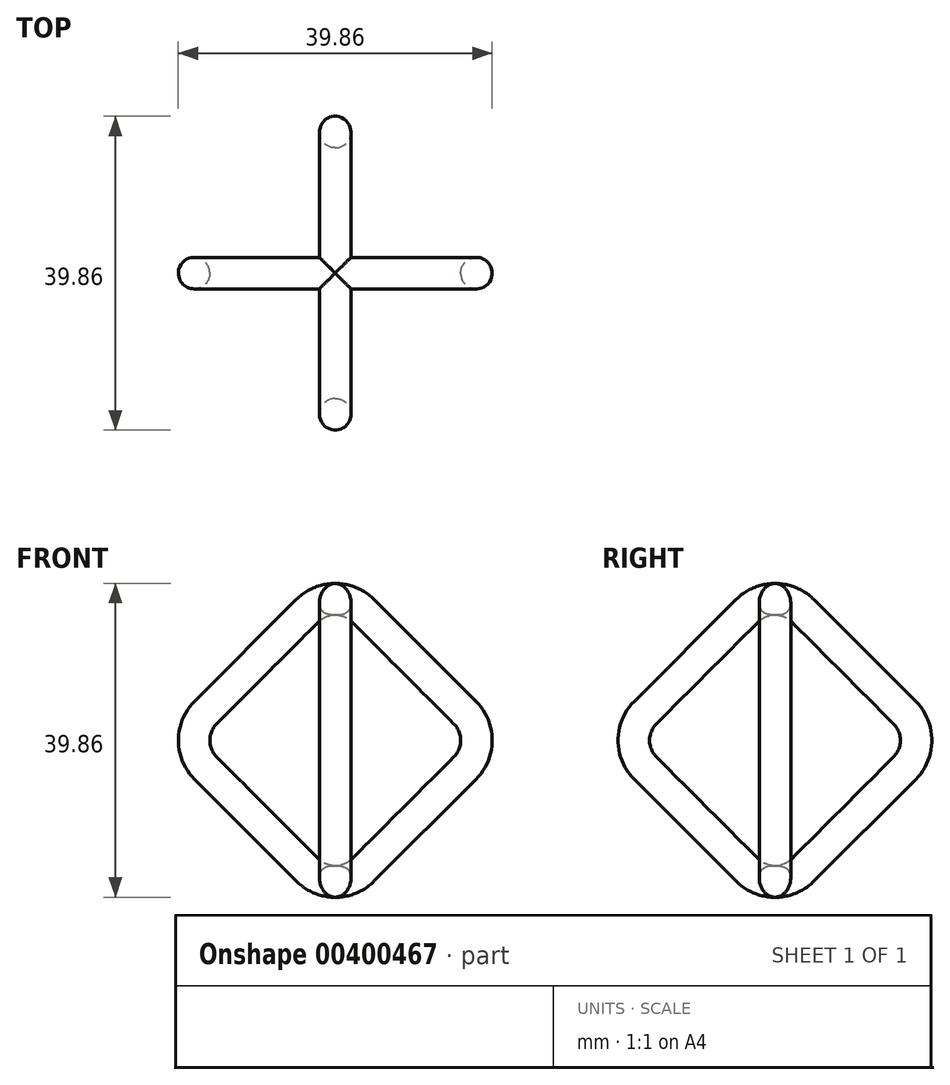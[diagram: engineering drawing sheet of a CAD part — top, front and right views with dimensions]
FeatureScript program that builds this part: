
annotation { "Feature Type Name" : "Feature", "Feature Type Description" : "" }
export const myFeature = defineFeature(function(context is Context, id is Id, definition is map)
    precondition{}
    {
        {
            var Q0;
            Q0=qCreatedBy(makeId("Front.planeOp"),FACE);
            var sketch = newSketch(context, id + "F0", { "sketchPlane" : qUnion([Q0])});
            skLineSegment(sketch, "E0", {"start": v(-3.54, 16.46) * mm, "end": v(-16.46, 3.54) * mm});
            skLineSegment(sketch, "E1", {"start": v(16.46, 3.54) * mm, "end": v(3.54, 16.46) * mm});
            skLineSegment(sketch, "E2", {"start": v(-20, 0) * mm, "end": v(20, 0) * mm, "construction": true});
            skPoint(sketch, "E3.visualSharp", {"position": v(0, 20) * mm});
            skArc(sketch, "E3.filletArc", {"start": v(3.54, 16.46) * mm, "mid": v(0, 17.93) * mm, "end": v(-3.54, 16.46) * mm});
            skPoint(sketch, "E4.visualSharp", {"position": v(20, 0) * mm});
            skArc(sketch, "E4.filletArc", {"start": v(17.93, 0) * mm, "mid": v(17.55, 1.91) * mm, "end": v(16.46, 3.54) * mm});
            skPoint(sketch, "E5.visualSharp", {"position": v(0, -20) * mm});
            skPoint(sketch, "E6.visualSharp", {"position": v(-20, 0) * mm});
            skArc(sketch, "E6.filletArc", {"start": v(-16.46, 3.54) * mm, "mid": v(-17.55, 1.91) * mm, "end": v(-17.93, 0) * mm});
            skLineSegment(sketch, "E7", {"start": v(-17.93, 0) * mm, "end": v(-17.93, -3.85) * mm, "construction": true});
            skLineSegment(sketch, "E8", {"start": v(17.93, 0) * mm, "end": v(17.93, -3.7) * mm, "construction": true});
            skSolve(sketch);
        }
        {
            var Q0;
            Q0=qCreatedBy(makeId("Top.planeOp"),FACE);
            var sketch = newSketch(context, id + "F1", { "sketchPlane" : qUnion([Q0])});
            skCircle(sketch, "E9", {"center": v(-17.93, 0) * mm, "radius": 2 * mm});
            skSolve(sketch);
        }
        {
            var Q0;
            Q0 = qSketchRegion(id + "F1", true);
            var Q1;
            Q1 = qConstructionFilter(qBodyType(qCreatedBy(id + "F0" ,EDGE), BodyType.WIRE), ConstructionObject.NO);
            sweep(context, id + "F2", {"profiles" : qUnion([Q0]), "path" : qUnion([Q1])});
        }
        {
            var Q0;
            Q0=makeQuery(id+"F2.opSweep","SWEPT_BODY",BODY,{"disambiguationData":[OSD([sQuery(id+"F0.wireOp",EDGE,"E4.filletArc"),sQuery(id+"F1.wireOp",EDGE,"E9")])]});
            var Q1;
            Q1=makeQuery(id+"F2.opSweep","CAP_FACE",FACE,{"disambiguationData":[OSD([sQuery(id+"F0.wireOp",VERTEX,"E6.filletArc.end"),sQuery(id+"F1.wireOp",EDGE,"E9")])],"isStart":true});
            mirror(context, id + "F3", {"operationType" : NewBodyOperationType.ADD, "entities" : qUnion([Q0]), "mirrorPlane" : qUnion([Q1])});
        }
        {
            var Q0;
            Q0=qCreatedBy(makeId("Front.planeOp"),FACE);
            var sketch = newSketch(context, id + "F4", { "sketchPlane" : qUnion([Q0])});
            skLineSegment(sketch, "E10", {"start": v(0, 0) * mm, "end": v(0, 22.8) * mm});
            skSolve(sketch);
        }
        {
            var Q0;
            Q0=makeQuery(id+"F2.opSweep","SWEPT_BODY",BODY,{"disambiguationData":[OSD([sQuery(id+"F0.wireOp",EDGE,"E4.filletArc"),sQuery(id+"F1.wireOp",EDGE,"E9")])]});
            var Q1;
            Q1=sQuery(id+"F4.wireOp",EDGE,"E10");
            circularPattern(context, id + "F5", {"operationType" : NewBodyOperationType.ADD, "entities" : qUnion([Q0]), "axis" : qUnion([Q1]), "angle" : 90 * degree, "instanceCount" : 2, "equalSpace" : true, "computeTransformsWithoutBuiltin" : true});
        }
    });
